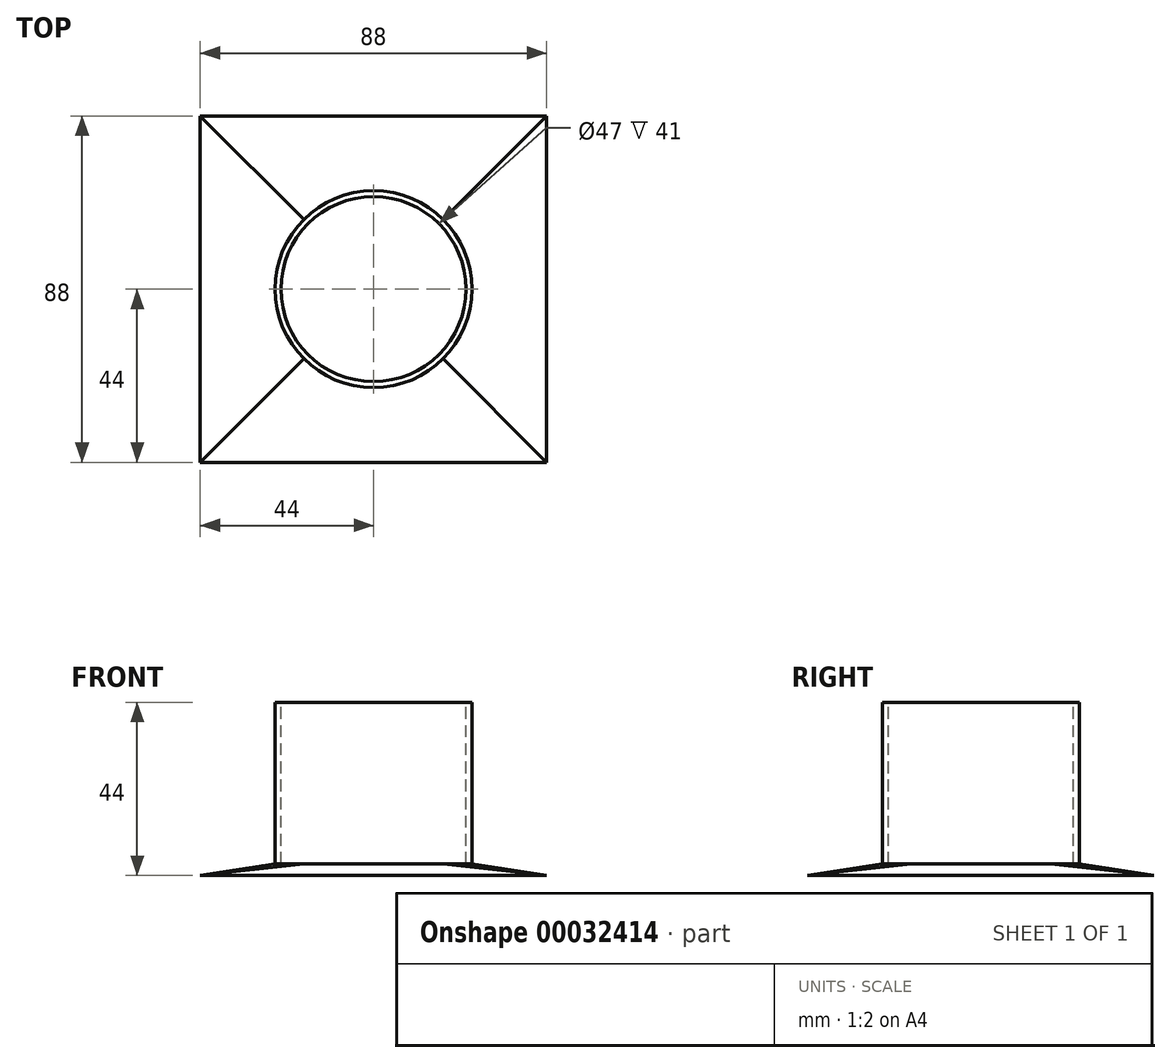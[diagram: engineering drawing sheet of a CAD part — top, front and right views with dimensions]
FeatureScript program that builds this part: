
annotation { "Feature Type Name" : "Feature", "Feature Type Description" : "" }
export const myFeature = defineFeature(function(context is Context, id is Id, definition is map)
    precondition{}
    {
        {
            var Q0;
            Q0=qCreatedBy(makeId("Top.planeOp"),FACE);
            var sketch = newSketch(context, id + "F0", { "sketchPlane" : qUnion([Q0])});
            skCircle(sketch, "E0", {"center": v(0, 0) * mm, "radius": 44 * mm});
            skSolve(sketch);
        }
        {
            var Q0;
            Q0=makeQuery(id+"F0.imprint","IMPRINT",FACE,{"disambiguationData":[TD([[makeQuery(id+"F0.imprint","IMPRINT",EDGE,{"derivedFrom":sQuery(id+"F0.wireOp",EDGE,"E0")}),1.0]])]});
            extrude(context, id + "F1", {"entities" : qUnion([Q0]), "depth" : 3 * mm});
        }
        {
            var Q0;
            Q0=makeQuery(id+"F1.opExtrude","SWEPT_BODY",BODY,{"disambiguationData":[OSD([sQuery(id+"F0.wireOp",EDGE,"E0")])]});
            deleteBodies(context, id + "F2", {"entities" : qUnion([Q0])});
        }
        {
            var Q0;
            Q0=qCreatedBy(makeId("Front.planeOp"),FACE);
            var sketch = newSketch(context, id + "F3", { "sketchPlane" : qUnion([Q0])});
            skLineSegment(sketch, "E1", {"start": v(0, 0) * mm, "end": v(0, 44) * mm});
            skLineSegment(sketch, "E2", {"start": v(0, 0) * mm, "end": v(0, 3) * mm});
            skLineSegment(sketch, "E3", {"start": v(0, 44) * mm, "end": v(25, 44) * mm});
            skLineSegment(sketch, "E4", {"start": v(25, 3) * mm, "end": v(25, 44) * mm});
            skLineSegment(sketch, "E5", {"start": v(0, 3) * mm, "end": v(25, 3) * mm});
            skSolve(sketch);
        }
        {
            var Q0;
            Q0=makeQuery(id+"F3.imprint","IMPRINT",FACE,{"disambiguationData":[TD([[makeQuery(id+"F3.imprint","IMPRINT",EDGE,{"derivedFrom":sQuery(id+"F3.wireOp",EDGE,"E1")}),-1.0]])]});
            var Q1;
            Q1=sQuery(id+"F3.wireOp",EDGE,"E1");
            revolve(context, id + "F4", {"entities" : qUnion([Q0]), "axis" : qUnion([Q1]), "revolveType" : RevolveType.FULL});
        }
        {
            var Q0;
            Q0=qCreatedBy(makeId("Top.planeOp"),FACE);
            var sketch = newSketch(context, id + "F5", { "sketchPlane" : qUnion([Q0])});
            skLineSegment(sketch, "E6.rect.bottom", {"start": v(44, -44) * mm, "end": v(-44, -44) * mm});
            skLineSegment(sketch, "E6.rect.top", {"start": v(44, 44) * mm, "end": v(-44, 44) * mm});
            skLineSegment(sketch, "E6.rect.left", {"start": v(44, -44) * mm, "end": v(44, 44) * mm});
            skLineSegment(sketch, "E6.rect.right", {"start": v(-44, -44) * mm, "end": v(-44, 44) * mm});
            skPoint(sketch, "E6.rect.middle", {"position": v(0, 0) * mm});
            skSolve(sketch);
        }
        {
            var Q0;
            Q0=makeQuery(id+"F4.opRevolve","SWEPT_FACE",FACE,{"disambiguationData":[OSD([sQuery(id+"F3.wireOp",EDGE,"E5")])]});
            var sketch = newSketch(context, id + "F6", { "sketchPlane" : qUnion([Q0])});
            skCircle(sketch, "E7", {"center": v(0, 0) * mm, "radius": 25 * mm});
            skSolve(sketch);
        }
        {
            var Q0;
            Q0 = qSketchRegion(id + "F6", true);
            var Q1;
            Q1=makeQuery(id+"F5.imprint","IMPRINT",FACE,{"disambiguationData":[TD([[makeQuery(id+"F5.imprint","IMPRINT",EDGE,{"derivedFrom":sQuery(id+"F5.wireOp",EDGE,"E6.rect.bottom")}),-1.0]])]});
            loft(context, id + "F7", {"operationType" : NewBodyOperationType.ADD, "sheetProfilesArray" : [{ "sheetProfileEntities" : qUnion([Q0]) }, { "sheetProfileEntities" : qUnion([Q1]) }]});
        }
        {
            var Q0;
            Q0=makeQuery(id+"F4.opRevolve","SWEPT_FACE",FACE,{"disambiguationData":[OSD([sQuery(id+"F3.wireOp",EDGE,"E3")])]});
            var sketch = newSketch(context, id + "F8", { "sketchPlane" : qUnion([Q0])});
            skCircle(sketch, "E8", {"center": v(0, 0) * mm, "radius": 23.5 * mm});
            skSolve(sketch);
        }
        {
            var Q0;
            Q0=makeQuery(id+"F8.imprint","IMPRINT",FACE,{"disambiguationData":[TD([[makeQuery(id+"F8.imprint","IMPRINT",EDGE,{"derivedFrom":sQuery(id+"F8.wireOp",EDGE,"E8")}),1.0]])]});
            extrude(context, id + "F9", {"entities" : qUnion([Q0]), "operationType" : NewBodyOperationType.REMOVE, "oppositeDirection" : true, "depth" : 41 * mm});
        }
    });
